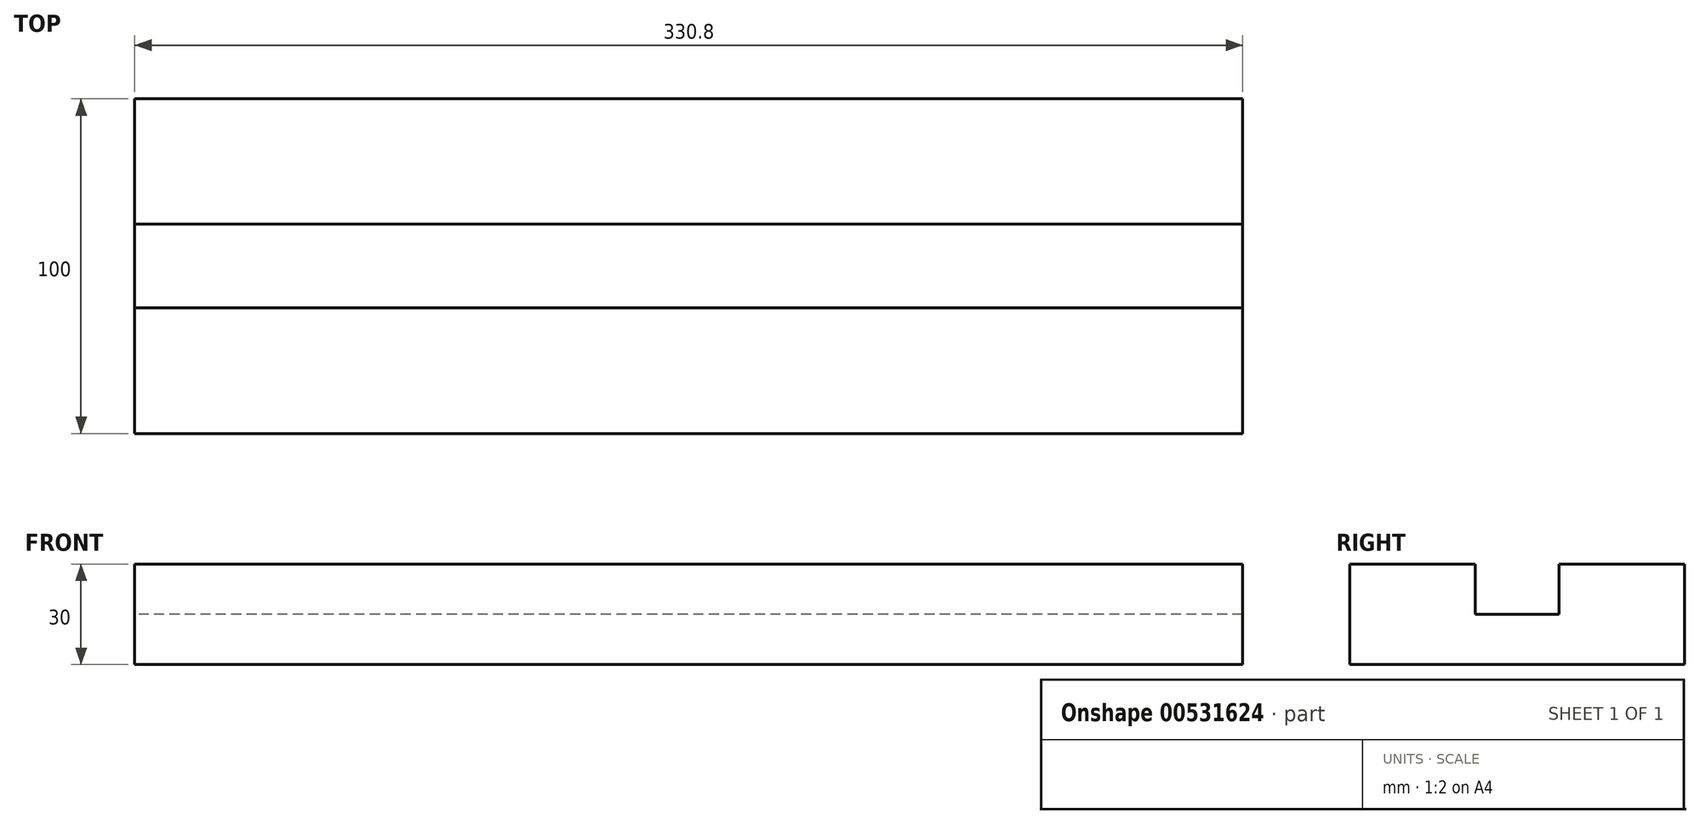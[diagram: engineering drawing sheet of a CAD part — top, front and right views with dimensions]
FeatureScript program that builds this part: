
annotation { "Feature Type Name" : "Feature", "Feature Type Description" : "" }
export const myFeature = defineFeature(function(context is Context, id is Id, definition is map)
    precondition{}
    {
        {
            var Q0;
            Q0=qCreatedBy(makeId("Right.planeOp"),FACE);
            var sketch = newSketch(context, id + "F0", { "sketchPlane" : qUnion([Q0])});
            skLineSegment(sketch, "E0", {"start": v(-50, 0) * mm, "end": v(50, 0) * mm});
            skLineSegment(sketch, "E1", {"start": v(50, 0) * mm, "end": v(50, 30) * mm});
            skLineSegment(sketch, "E2", {"start": v(50, 30) * mm, "end": v(12.5, 30) * mm});
            skLineSegment(sketch, "E3", {"start": v(12.5, 30) * mm, "end": v(12.5, 15) * mm});
            skLineSegment(sketch, "E4", {"start": v(12.5, 15) * mm, "end": v(-12.5, 15) * mm});
            skLineSegment(sketch, "E5", {"start": v(-12.5, 15) * mm, "end": v(-12.5, 30) * mm});
            skLineSegment(sketch, "E6", {"start": v(-12.5, 30) * mm, "end": v(-50, 30) * mm});
            skLineSegment(sketch, "E7", {"start": v(-50, 30) * mm, "end": v(-50, 0) * mm});
            skLineSegment(sketch, "E8", {"start": v(0, 0) * mm, "end": v(0, 15) * mm, "construction": true});
            skSolve(sketch);
        }
        {
            var Q0;
            Q0=qSketchRegion(id+"F0",true);
            extrude(context, id + "F1", {"entities" : qUnion([Q0]), "depth" : 330.8 * mm});
        }
    });
